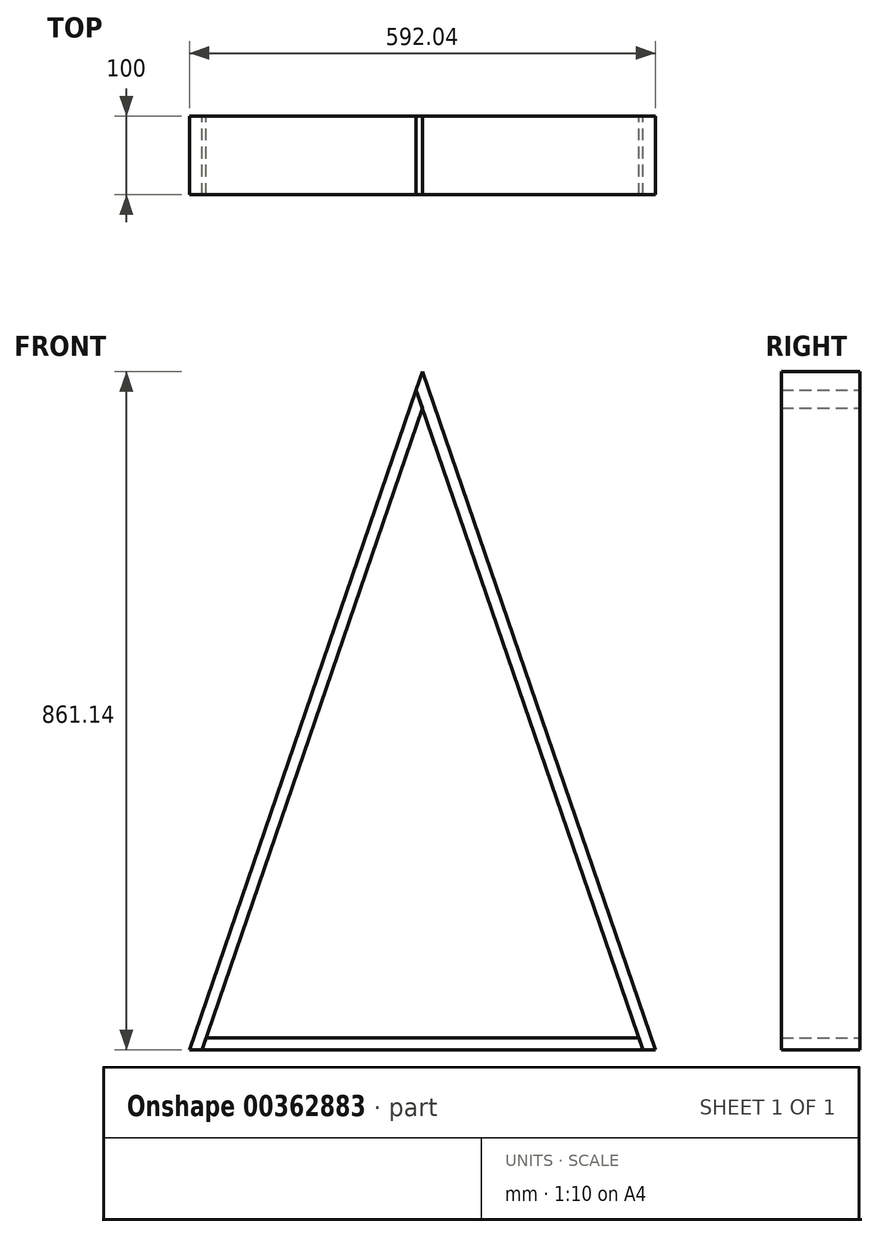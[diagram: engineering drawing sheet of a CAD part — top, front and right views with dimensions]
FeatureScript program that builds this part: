
annotation { "Feature Type Name" : "Feature", "Feature Type Description" : "" }
export const myFeature = defineFeature(function(context is Context, id is Id, definition is map)
    precondition{}
    {
        {
            var Q0;
            Q0=qCreatedBy(makeId("Front.planeOp"),FACE);
            var sketch = newSketch(context, id + "F0", { "sketchPlane" : qUnion([Q0])});
            skLineSegment(sketch, "E0", {"start": v(0, 0) * mm, "end": v(0, -800) * mm, "construction": true});
            skLineSegment(sketch, "E1", {"start": v(0, -800) * mm, "end": v(-275, -800) * mm});
            skLineSegment(sketch, "E2", {"start": v(-275, -800) * mm, "end": v(0, 0) * mm});
            skLineSegment(sketch, "E3.0", {"start": v(-296.02, -815) * mm, "end": v(0, 46.14) * mm});
            skLineSegment(sketch, "E4.0", {"start": v(0, -815) * mm, "end": v(-296.02, -815) * mm});
            skLineSegment(sketch, "E5.MirrorCS", {"start": v(296.02, -815) * mm, "end": v(0, 46.14) * mm});
            skLineSegment(sketch, "E6.MirrorCS", {"start": v(275, -800) * mm, "end": v(0, 0) * mm});
            skLineSegment(sketch, "E7.MirrorCS", {"start": v(0, -815) * mm, "end": v(296.02, -815) * mm});
            skLineSegment(sketch, "E8.MirrorCS", {"start": v(0, -800) * mm, "end": v(275, -800) * mm});
            skLineSegment(sketch, "E9", {"start": v(0, 0) * mm, "end": v(-7.93, 23.07) * mm});
            skLineSegment(sketch, "E10", {"start": v(-275, -800) * mm, "end": v(-280.16, -815) * mm});
            skLineSegment(sketch, "E11", {"start": v(275, -800) * mm, "end": v(280.16, -815) * mm});
            skSolve(sketch);
        }
        {
            var Q0;
            Q0=makeQuery(id+"F0.imprint","IMPRINT",FACE,{"disambiguationData":[TD([[makeQuery(id+"F0.imprint","IMPRINT",EDGE,{"derivedFrom":sQuery(id+"F0.wireOp",EDGE,"E2")}),1.0]])]});
            extrude(context, id + "F1", {"entities" : qUnion([Q0]), "depth" : 100 * mm});
        }
        {
            var Q0;
            {var subQ1=sQuery(id+"F0.wireOp",EDGE,"E5.MirrorCS");Q0=makeQuery(id+"F0.imprint","IMPRINT",FACE,{"disambiguationData":[TD([[makeQuery(id+"F0.imprint","IMPRINT",EDGE,{"derivedFrom":subQ1}),1.0]])]});}
            extrude(context, id + "F2", {"entities" : qUnion([Q0]), "depth" : 100 * mm});
        }
        {
            var Q0;
            Q0=makeQuery(id+"F0.imprint","IMPRINT",FACE,{"disambiguationData":[TD([[makeQuery(id+"F0.imprint","IMPRINT",EDGE,{"derivedFrom":sQuery(id+"F0.wireOp",EDGE,"E1")}),1.0]])]});
            var Q1;
            Q1=sQuery(id+"F0.wireOp",EDGE,"E9");
            extrude(context, id + "F3", {"entities" : qUnion([Q0]), "surfaceEntities" : qUnion([Q1]), "depth" : 100 * mm});
        }
    });
